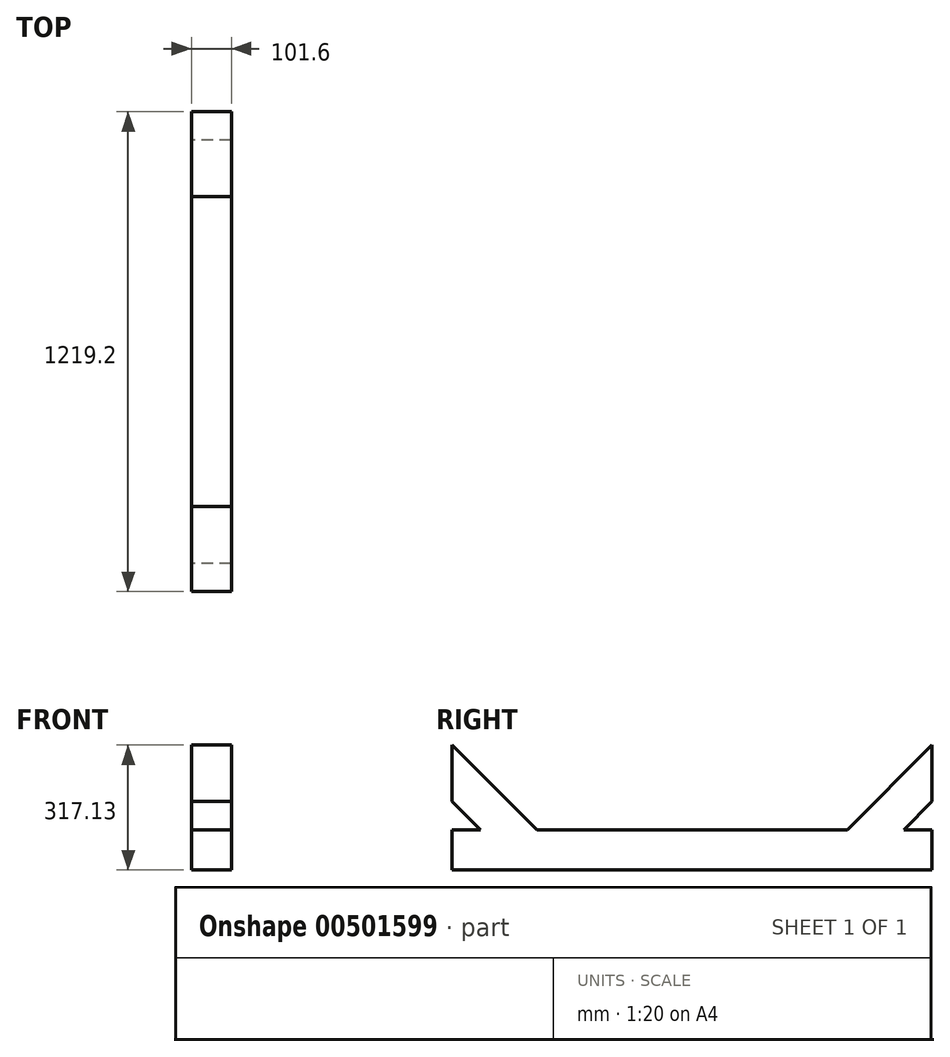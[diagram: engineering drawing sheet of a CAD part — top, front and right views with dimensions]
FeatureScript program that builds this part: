
annotation { "Feature Type Name" : "Feature", "Feature Type Description" : "" }
export const myFeature = defineFeature(function(context is Context, id is Id, definition is map)
    precondition{}
    {
        {
            var Q0;
            Q0=qCreatedBy(makeId("Right.planeOp"),FACE);
            var sketch = newSketch(context, id + "F0", { "sketchPlane" : qUnion([Q0])});
            skLineSegment(sketch, "E0.bottom", {"start": v(-609.6, 56.56) * mm, "end": v(609.6, 56.56) * mm});
            skLineSegment(sketch, "E0.top", {"start": v(-609.6, -45.04) * mm, "end": v(609.6, -45.04) * mm});
            skLineSegment(sketch, "E0.left", {"start": v(-609.6, 56.56) * mm, "end": v(-609.6, -45.04) * mm});
            skLineSegment(sketch, "E0.right", {"start": v(609.6, 56.56) * mm, "end": v(609.6, -45.04) * mm});
            skLineSegment(sketch, "E1", {"start": v(-609.6, 56.56) * mm, "end": v(-609.6, 531.34) * mm});
            skLineSegment(sketch, "E2", {"start": v(-609.6, 272.09) * mm, "end": v(-394.07, 56.56) * mm});
            skLineSegment(sketch, "E3", {"start": v(-609.6, 128.4) * mm, "end": v(-537.76, 56.56) * mm});
            skLineSegment(sketch, "E4", {"start": v(0, -45.04) * mm, "end": v(0, 329.77) * mm});
            skLineSegment(sketch, "E5.MirrorCS", {"start": v(609.6, 272.09) * mm, "end": v(394.07, 56.56) * mm});
            skLineSegment(sketch, "E6.MirrorCS", {"start": v(609.6, 128.4) * mm, "end": v(537.76, 56.56) * mm});
            skLineSegment(sketch, "E7.MirrorCS", {"start": v(609.6, 56.56) * mm, "end": v(609.6, 531.34) * mm});
            skSolve(sketch);
        }
        {
            var Q0;
            {var subQ0=sQuery(id+"F0.wireOp",EDGE,"E2");Q0=makeQuery(id+"F0.imprint","IMPRINT",FACE,{"disambiguationData":[TD([[makeQuery(id+"F0.imprint","IMPRINT",EDGE,{"derivedFrom":subQ0}),-1.0]])]});}
            var Q1;
            {var subQ4=sQuery(id+"F0.wireOp",EDGE,"E0.left");Q1=makeQuery(id+"F0.imprint","IMPRINT",FACE,{"disambiguationData":[TD([[makeQuery(id+"F0.imprint","IMPRINT",EDGE,{"derivedFrom":subQ4}),1.0]])]});}
            var Q2;
            {var subQ0=sQuery(id+"F0.wireOp",EDGE,"E5.MirrorCS");Q2=makeQuery(id+"F0.imprint","IMPRINT",FACE,{"disambiguationData":[TD([[makeQuery(id+"F0.imprint","IMPRINT",EDGE,{"derivedFrom":subQ0}),1.0]])]});}
            var Q3;
            {var subQ0=sQuery(id+"F0.wireOp",EDGE,"E0.right");Q3=makeQuery(id+"F0.imprint","IMPRINT",FACE,{"disambiguationData":[TD([[makeQuery(id+"F0.imprint","IMPRINT",EDGE,{"derivedFrom":subQ0}),-1.0]])]});}
            extrude(context, id + "F1", {"entities" : qUnion([Q0, Q1, Q2, Q3]), "depth" : 101.6 * mm, "offsetDistance" : 25.4 * mm});
        }
    });
